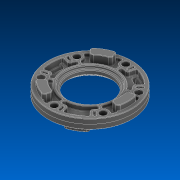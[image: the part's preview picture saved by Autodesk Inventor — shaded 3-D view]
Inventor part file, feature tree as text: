
AUTODESK INVENTOR PART (.ipt)
format: ipt  version: 2022.2 (Build 262287000, 287)  size: 1,699,840 bytes
history: native  units: in
note: dims shown in document units (in); Inventor stores cm internally (conversion verified against a paired STEP export)
features: fillet x1
ambient origin geometry x8: Origin, YZ Plane, XZ Plane, XY Plane, X Axis, Y Axis, Z Axis, Center Point
bodies: Solid1 (feature_tree)
feature tree (1):
  fillet  "Fillet10"  [1 undecoded]
note: 1 required parameter value undecoded (feature->parameter linkage not recoverable at this tier; creation-order binding heuristic only, values carry confidence <= 0.55)
